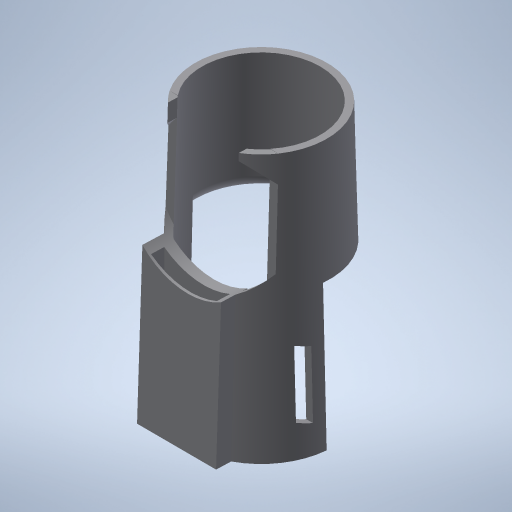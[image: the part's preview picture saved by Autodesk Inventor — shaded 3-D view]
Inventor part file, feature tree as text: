
AUTODESK INVENTOR PART (.ipt)
format: ipt  version: 2024 (Build 280153000, 153)  size: 412,160 bytes
history: native  units: mm
features: sketch x6, plane x5, extrude x5, fillet x2, projected_geometry x2, revolve x1
ambient origin geometry x8: Origin, YZ Plane, XZ Plane, XY Plane, X Axis, Y Axis, Z Axis, Center Point
bodies: Solid1 (feature_tree)
feature tree (21):
  revolve  "Revolution1"  [1 undecoded]
  plane  "Work Plane1"
  extrude  "Extrusion1"  TaperAngle=90.0deg  [1 undecoded]
  fillet  "Fillet1"  [1 undecoded]
  fillet  "Fillet2"  Radius=20.0mm
  plane  "Work Plane4"
  sketch  "Sketch4"  dims[d8=12.0mm d9=0.0mm d10=2.0mm]
  extrude  "Extrusion3"  Depth=2.0mm
  extrude  "Extrusion4"  Depth=15.358897mm
  sketch  "Sketch5"  dims[d11=2.0mm d14=15.358897mm d15=11.0mm]
  plane  "Work Plane5"
  extrude  "Extrusion7"  Depth=12.0mm
  plane  "Work Plane6"
  extrude  "Extrusion8"  Depth=4.0mm TaperAngle=0.0deg
  sketch  "Sketch1"  dims[d1=40.0mm d2=10.0mm]
  sketch  "Sketch2"  dims[d3=11.0mm d5=90.0deg d6=-11.0mm d7=20.0mm]
  projected_geometry  "Projected Loop1"
  plane  "Work Plane3"
  projected_geometry  "Projected Loop2"
  sketch  "Sketch6"  dims[d16=40.0mm d17=12.0mm]
  sketch  "Sketch7"  dims[d18=40.0mm d22=4.0mm d23=0.0mm d24=20.0mm d25=5.0mm d26=0.0mm d27=12.0mm d28=1.0mm d29=10.0mm d30=2.0mm d35=-0.25mm d36=40.0mm d37=0.0mm d38=-20.75mm d39=10.0mm d43=10.0mm d44=2.0mm d45=10.0mm d46=0.0mm d40=0.5mm d41=0.872665mm]
note: 3 required parameter values undecoded (feature->parameter linkage not recoverable at this tier; creation-order binding heuristic only, values carry confidence <= 0.55)